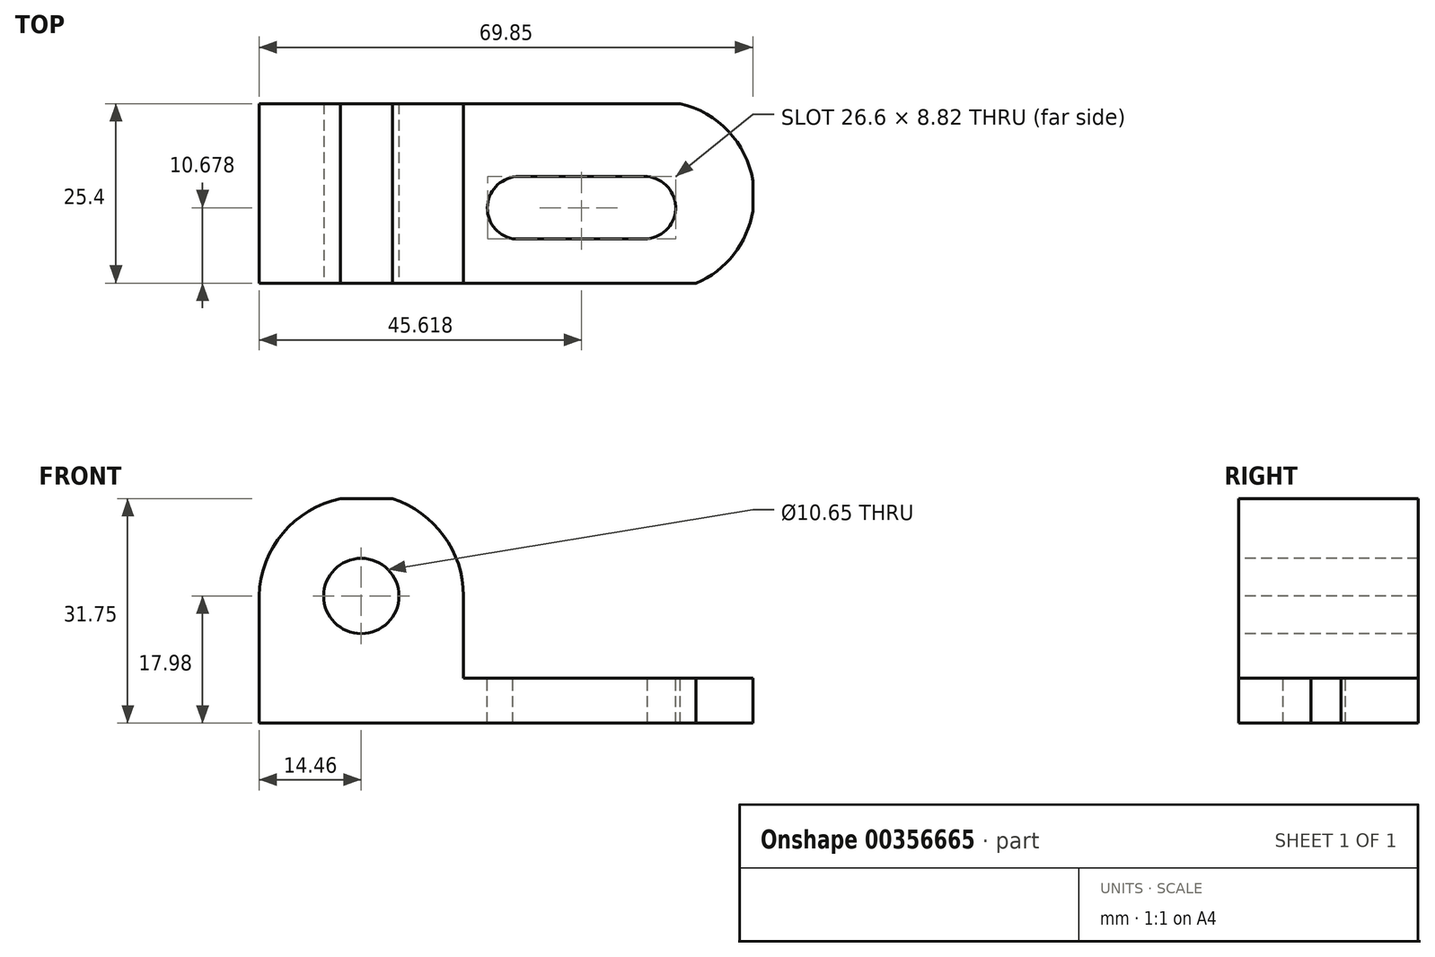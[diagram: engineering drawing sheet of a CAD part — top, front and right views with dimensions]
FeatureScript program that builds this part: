
annotation { "Feature Type Name" : "Feature", "Feature Type Description" : "" }
export const myFeature = defineFeature(function(context is Context, id is Id, definition is map)
    precondition{}
    {
        {
            var Q0;
            Q0=qCreatedBy(makeId("Front.planeOp"),FACE);
            var sketch = newSketch(context, id + "F0", { "sketchPlane" : qUnion([Q0])});
            skLineSegment(sketch, "E0.bottom", {"start": v(-28.92, -17.98) * mm, "end": v(40.93, -17.98) * mm});
            skLineSegment(sketch, "E0.top", {"start": v(-28.92, 13.77) * mm, "end": v(40.93, 13.77) * mm});
            skLineSegment(sketch, "E0.left", {"start": v(-28.92, -17.98) * mm, "end": v(-28.92, 13.77) * mm});
            skLineSegment(sketch, "E0.right", {"start": v(40.93, -17.98) * mm, "end": v(40.93, 13.77) * mm});
            skSolve(sketch);
        }
        {
            var Q0;
            Q0=makeQuery(id+"F0.imprint","IMPRINT",FACE,{"disambiguationData":[TD([[makeQuery(id+"F0.imprint","IMPRINT",EDGE,{"derivedFrom":sQuery(id+"F0.wireOp",EDGE,"E0.bottom")}),1.0]])]});
            extrude(context, id + "F1", {"entities" : qUnion([Q0]), "depth" : 25.4 * mm});
        }
        {
            var Q0;
            Q0=makeQuery(id+"F1.opExtrude","CAP_FACE",FACE,{"disambiguationData":[OSD([sQuery(id+"F0.wireOp",EDGE,"E0.bottom"),sQuery(id+"F0.wireOp",EDGE,"E0.top"),sQuery(id+"F0.wireOp",EDGE,"E0.left"),sQuery(id+"F0.wireOp",EDGE,"E0.right")])],"isStart":false});
            var sketch = newSketch(context, id + "F2", { "sketchPlane" : qUnion([Q0])});
            skArc(sketch, "E1", {"start": v(0, 0) * mm, "mid": v(-14.46, 14.07) * mm, "end": v(-28.92, 0) * mm});
            skLineSegment(sketch, "E2", {"start": v(0, 0) * mm, "end": v(0, -17.98) * mm});
            skLineSegment(sketch, "E3", {"start": v(0, -17.98) * mm, "end": v(-28.92, -17.98) * mm});
            skLineSegment(sketch, "E4", {"start": v(-28.92, -17.98) * mm, "end": v(-28.92, 0) * mm});
            skSolve(sketch);
        }
        {
            var Q0;
            {var subQ1=makeQuery(id+"F1.opExtrude","CAP_EDGE",EDGE,{"disambiguationData":[OSD([sQuery(id+"F0.wireOp",EDGE,"E0.left")])],"isStart":false});var subQ3=makeQuery(id+"F1.opExtrude","CAP_EDGE",EDGE,{"disambiguationData":[OSD([sQuery(id+"F0.wireOp",EDGE,"E0.top")])],"isStart":false});var subQ5=makeQuery(id+"F2.imprint","INTERSECT",VERTEX,{"derivedFrom":[subQ3,subQ1]});Q0=makeQuery(id+"F2.imprint","IMPRINT",FACE,{"disambiguationData":[TD([[makeQuery(id+"F2.imprint","IMPRINT",EDGE,{"disambiguationData":[TD([[subQ5,-1.0]])],"derivedFrom":subQ3}),-1.0]])]});}
            extrude(context, id + "F3", {"entities" : qUnion([Q0]), "operationType" : NewBodyOperationType.REMOVE, "oppositeDirection" : true, "depth" : 25.4 * mm});
        }
        {
            var Q0;
            Q0=makeQuery(id+"F1.opExtrude","CAP_FACE",FACE,{"disambiguationData":[OSD([sQuery(id+"F0.wireOp",EDGE,"E0.bottom"),sQuery(id+"F0.wireOp",EDGE,"E0.top"),sQuery(id+"F0.wireOp",EDGE,"E0.left"),sQuery(id+"F0.wireOp",EDGE,"E0.right")])],"isStart":false});
            var sketch = newSketch(context, id + "F4", { "sketchPlane" : qUnion([Q0])});
            skLineSegment(sketch, "E5", {"start": v(40.93, 13.77) * mm, "end": v(0, 13.77) * mm});
            skLineSegment(sketch, "E6", {"start": v(0, 13.77) * mm, "end": v(0, -11.63) * mm});
            skLineSegment(sketch, "E7", {"start": v(0, -11.63) * mm, "end": v(40.93, -11.63) * mm});
            skLineSegment(sketch, "E8", {"start": v(40.93, -11.63) * mm, "end": v(40.93, 13.77) * mm});
            skSolve(sketch);
        }
        {
            var Q0;
            Q0=makeQuery(id+"F4.imprint","IMPRINT",FACE,{"disambiguationData":[TD([[makeQuery(id+"F4.imprint","IMPRINT",EDGE,{"derivedFrom":sQuery(id+"F4.wireOp",EDGE,"E5")}),-1.0]])]});
            extrude(context, id + "F5", {"entities" : qUnion([Q0]), "operationType" : NewBodyOperationType.REMOVE, "oppositeDirection" : true, "depth" : 25.4 * mm});
        }
        {
            var Q0;
            Q0=makeQuery(id+"F1.opExtrude","CAP_FACE",FACE,{"disambiguationData":[OSD([sQuery(id+"F0.wireOp",EDGE,"E0.bottom"),sQuery(id+"F0.wireOp",EDGE,"E0.top"),sQuery(id+"F0.wireOp",EDGE,"E0.left"),sQuery(id+"F0.wireOp",EDGE,"E0.right")])],"isStart":false});
            var sketch = newSketch(context, id + "F6", { "sketchPlane" : qUnion([Q0])});
            skArc(sketch, "E9", {"start": v(0, 0) * mm, "mid": v(-14.46, 14.46) * mm, "end": v(-28.92, 0) * mm});
            skSolve(sketch);
        }
        {
            var Q0;
            {var subQ0=sQuery(id+"F6.wireOp",EDGE,"E9");var subQ1=makeQuery(id+"F5.boolean.opBoolean","COPY",EDGE,{"derivedFrom":makeQuery(id+"F5.opExtrude","CAP_EDGE",EDGE,{"disambiguationData":[OSD([sQuery(id+"F4.wireOp",EDGE,"E6")])],"isStart":true})});var subQ2=makeQuery(id+"F6.imprint","INTERSECT",VERTEX,{"derivedFrom":[subQ1,subQ0]});Q0=makeQuery(id+"F6.imprint","IMPRINT",FACE,{"disambiguationData":[TD([[makeQuery(id+"F6.imprint","IMPRINT",EDGE,{"disambiguationData":[TD([[subQ2,-1.0]])],"derivedFrom":subQ0}),-1.0]])]});}
            extrude(context, id + "F7", {"entities" : qUnion([Q0]), "operationType" : NewBodyOperationType.REMOVE, "oppositeDirection" : true, "depth" : 25.4 * mm});
        }
        {
            var Q0;
            Q0=makeQuery(id+"F5.boolean.opBoolean","COPY",FACE,{"derivedFrom":makeQuery(id+"F5.opExtrude","SWEPT_FACE",FACE,{"disambiguationData":[OSD([sQuery(id+"F4.wireOp",EDGE,"E7")])]})});
            var sketch = newSketch(context, id + "F8", { "sketchPlane" : qUnion([Q0])});
            skArc(sketch, "E10", {"start": v(32.9, -25.4) * mm, "mid": v(40.47, -9) * mm, "end": v(24.8, 0) * mm});
            skSolve(sketch);
        }
        {
            var Q0;
            {var subQ0=sQuery(id+"F8.wireOp",EDGE,"E10");var subQ1=sQuery(id+"F4.wireOp",EDGE,"E7");var subQ2=makeQuery(id+"F5.boolean.opBoolean","COPY",EDGE,{"derivedFrom":makeQuery(id+"F5.opExtrude","CAP_EDGE",EDGE,{"disambiguationData":[OSD([subQ1])],"isStart":true})});var subQ3=makeQuery(id+"F8.imprint","INTERSECT",VERTEX,{"derivedFrom":[subQ2,subQ0]});Q0=makeQuery(id+"F8.imprint","IMPRINT",FACE,{"disambiguationData":[TD([[makeQuery(id+"F8.imprint","IMPRINT",EDGE,{"disambiguationData":[TD([[subQ3,-1.0]])],"derivedFrom":subQ0}),-1.0]])]});}
            var Q1;
            {var subQ0=sQuery(id+"F8.wireOp",EDGE,"E10");var subQ1=sQuery(id+"F4.wireOp",EDGE,"E7");var subQ4=makeQuery(id+"F5.boolean.opBoolean","COPY",EDGE,{"derivedFrom":makeQuery(id+"F5.opExtrude","CAP_EDGE",EDGE,{"disambiguationData":[OSD([subQ1])],"isStart":false})});var subQ5=makeQuery(id+"F8.imprint","INTERSECT",VERTEX,{"disambiguationData":[OD(1.0)],"derivedFrom":[subQ4,subQ0]});Q1=makeQuery(id+"F8.imprint","IMPRINT",FACE,{"disambiguationData":[TD([[makeQuery(id+"F8.imprint","IMPRINT",EDGE,{"disambiguationData":[TD([[subQ5,1.0]])],"derivedFrom":subQ0}),-1.0]])]});}
            extrude(context, id + "F9", {"entities" : qUnion([Q0, Q1]), "operationType" : NewBodyOperationType.REMOVE, "oppositeDirection" : true, "depth" : 25.4 * mm});
        }
        {
            var Q0;
            Q0=makeQuery(id+"F5.boolean.opBoolean","COPY",FACE,{"derivedFrom":makeQuery(id+"F5.opExtrude","SWEPT_FACE",FACE,{"disambiguationData":[OSD([sQuery(id+"F4.wireOp",EDGE,"E7")])]})});
            var sketch = newSketch(context, id + "F10", { "sketchPlane" : qUnion([Q0])});
            skLineSegment(sketch, "E11", {"start": v(26, -19.13) * mm, "end": v(6.94, -19.13) * mm});
            skLineSegment(sketch, "E12", {"start": v(7.83, -10.31) * mm, "end": v(25.58, -10.31) * mm});
            skArc(sketch, "E13", {"start": v(26, -19.13) * mm, "mid": v(30, -14.53) * mm, "end": v(25.58, -10.31) * mm});
            skArc(sketch, "E14", {"start": v(7.83, -10.31) * mm, "mid": v(3.4, -14.32) * mm, "end": v(6.94, -19.13) * mm});
            skSolve(sketch);
        }
        {
            var Q0;
            Q0=makeQuery(id+"F10.imprint","IMPRINT",FACE,{"disambiguationData":[TD([[makeQuery(id+"F10.imprint","IMPRINT",EDGE,{"derivedFrom":sQuery(id+"F10.wireOp",EDGE,"E11")}),-1.0]])]});
            extrude(context, id + "F11", {"entities" : qUnion([Q0]), "operationType" : NewBodyOperationType.REMOVE, "oppositeDirection" : true, "depth" : 25.4 * mm});
        }
        {
            var Q0;
            Q0=makeQuery(id+"F1.opExtrude","CAP_FACE",FACE,{"disambiguationData":[OSD([sQuery(id+"F0.wireOp",EDGE,"E0.bottom"),sQuery(id+"F0.wireOp",EDGE,"E0.top"),sQuery(id+"F0.wireOp",EDGE,"E0.left"),sQuery(id+"F0.wireOp",EDGE,"E0.right")])],"isStart":false});
            var sketch = newSketch(context, id + "F12", { "sketchPlane" : qUnion([Q0])});
            skCircle(sketch, "E15", {"center": v(-14.46, 0) * mm, "radius": 5.33 * mm});
            skSolve(sketch);
        }
        {
            var Q0;
            Q0=makeQuery(id+"F12.imprint","IMPRINT",FACE,{"disambiguationData":[TD([[makeQuery(id+"F12.imprint","IMPRINT",EDGE,{"derivedFrom":sQuery(id+"F12.wireOp",EDGE,"E15")}),1.0]])]});
            extrude(context, id + "F13", {"entities" : qUnion([Q0]), "operationType" : NewBodyOperationType.REMOVE, "oppositeDirection" : true, "depth" : 25.4 * mm});
        }
    });
